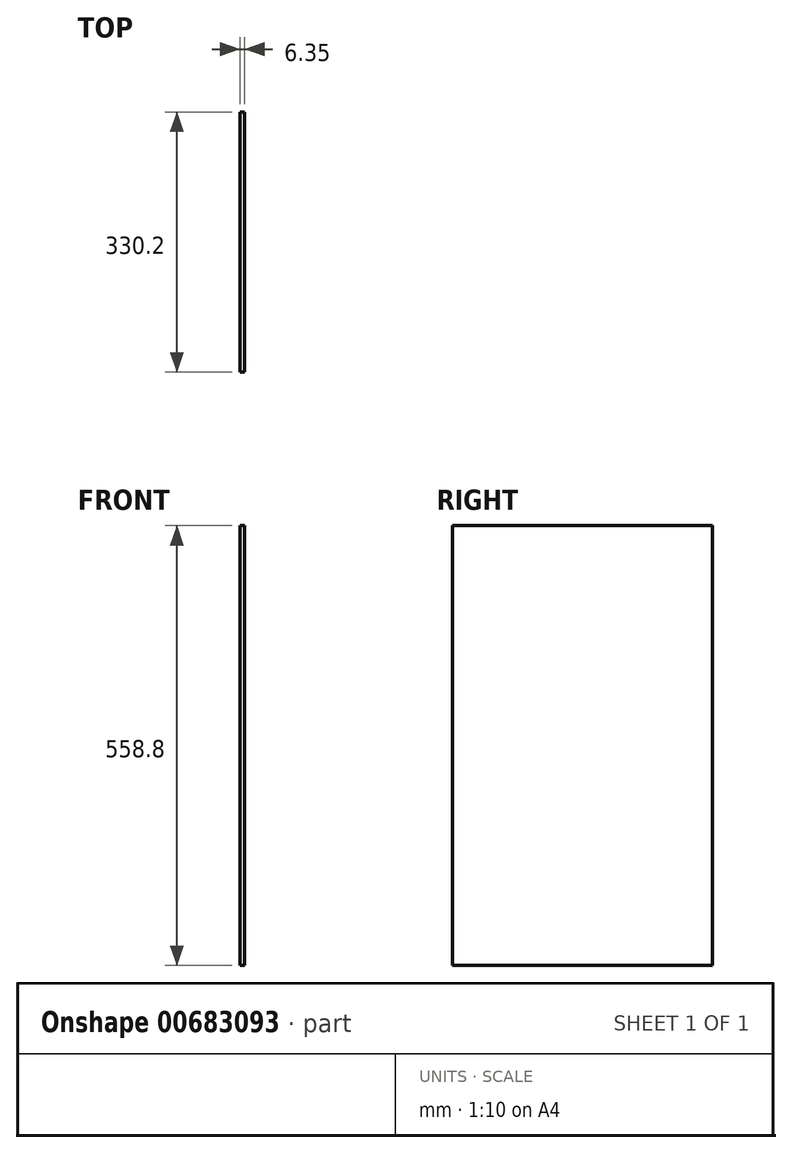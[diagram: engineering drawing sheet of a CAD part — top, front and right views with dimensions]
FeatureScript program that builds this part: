
annotation { "Feature Type Name" : "Feature", "Feature Type Description" : "" }
export const myFeature = defineFeature(function(context is Context, id is Id, definition is map)
    precondition{}
    {
        {
            var Q0;
            Q0=qCreatedBy(makeId("Right.planeOp"),FACE);
            var sketch = newSketch(context, id + "F0", { "sketchPlane" : qUnion([Q0])});
            skLineSegment(sketch, "E0.bottom", {"start": v(165.1, 279.4) * mm, "end": v(-165.1, 279.4) * mm});
            skLineSegment(sketch, "E0.top", {"start": v(165.1, -279.4) * mm, "end": v(-165.1, -279.4) * mm});
            skLineSegment(sketch, "E0.left", {"start": v(165.1, 279.4) * mm, "end": v(165.1, -279.4) * mm});
            skLineSegment(sketch, "E0.right", {"start": v(-165.1, 279.4) * mm, "end": v(-165.1, -279.4) * mm});
            skPoint(sketch, "E0.middle", {"position": v(0, 0) * mm});
            skSolve(sketch);
        }
        {
            var Q0;
            Q0 = qSketchRegion(id + "F0", true);
            extrude(context, id + "F1", {"entities" : qUnion([Q0]), "depth" : 6.35 * mm, "offsetDistance" : 25.4 * mm});
        }
    });
